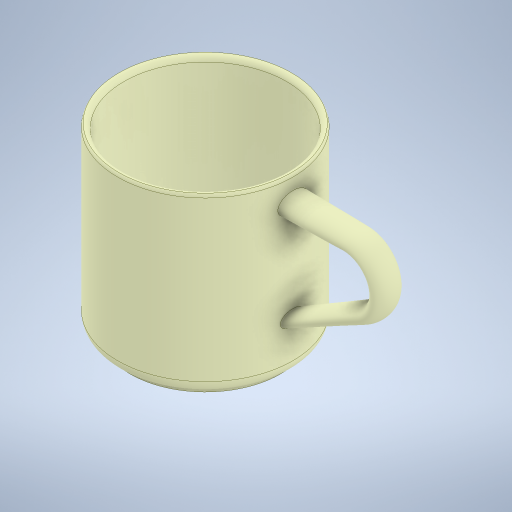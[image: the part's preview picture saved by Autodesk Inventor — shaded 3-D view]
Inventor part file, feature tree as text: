
AUTODESK INVENTOR PART (.ipt)
format: ipt  version: 2024 (Build 280153000, 153)  size: 357,888 bytes
history: native  units: mm
features: sketch x6, other x2, plane x2, revolve x1, loft x1, fillet x1, extrude x1
ambient origin geometry x8: Origin, YZ Plane, XZ Plane, XY Plane, X Axis, Y Axis, Z Axis, Center Point
bodies: Body1 (feature_tree)
feature tree (14):
  other  "Sección transversal1"
  other  "Sólido1"
  revolve  "Revolución1"  [1 undecoded]
  sketch  "Boceto2"  dims[d19=0.0mm d20=90.0deg d21=0.0mm d22=90.0deg d23=0.0mm d24=90.0deg]
  plane  "Plano de trabajo1"
  sketch  "Boceto3"  dims[d25=2.0mm d30=60.0mm]
  plane  "Plano de trabajo2"
  loft  "Solevación1"
  fillet  "Empalme1"  [1 undecoded]
  sketch  "Boceto5"  dims[d32=2.0mm d33=0.0mm]
  extrude  "Extrusión1"  Depth=2.0mm
  sketch  "Boceto1"  dims[d4=90.0deg d5=0.5mm d6=2.0mm d7=0.0mm d8=20.0mm]
  sketch  "Boceto4"  dims[d31=57.0mm]
  sketch  "Boceto6"
note: 2 required parameter values undecoded (feature->parameter linkage not recoverable at this tier; creation-order binding heuristic only, values carry confidence <= 0.55)